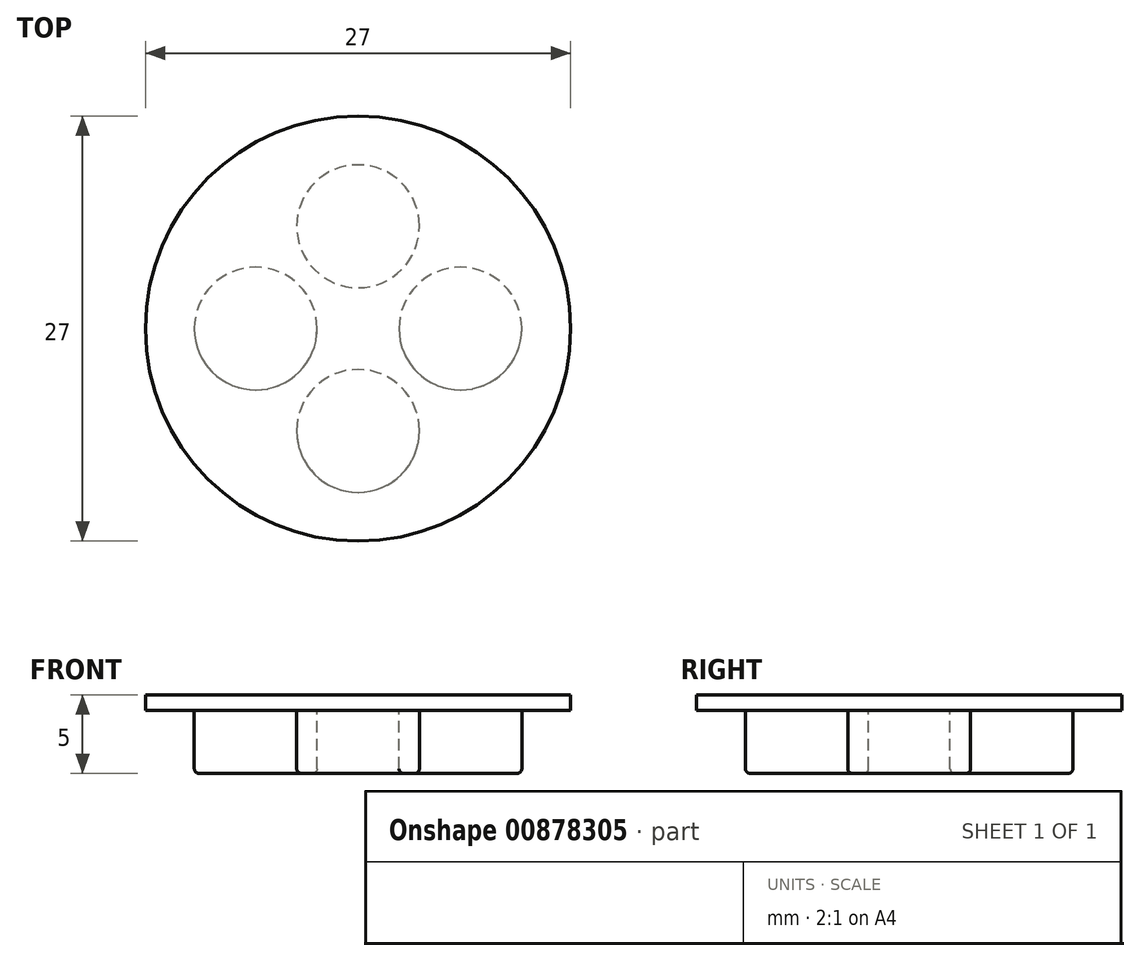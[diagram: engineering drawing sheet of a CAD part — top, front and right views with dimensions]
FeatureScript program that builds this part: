
annotation { "Feature Type Name" : "Feature", "Feature Type Description" : "" }
export const myFeature = defineFeature(function(context is Context, id is Id, definition is map)
    precondition{}
    {
        {
            var Q0;
            Q0=qCreatedBy(makeId("Top.planeOp"),FACE);
            var sketch = newSketch(context, id + "F0", { "sketchPlane" : qUnion([Q0])});
            skCircle(sketch, "E0", {"center": v(-69.13, 46.92) * mm, "radius": 13.5 * mm});
            skSolve(sketch);
        }
        {
            var Q0;
            Q0 = qSketchRegion(id + "F0", true);
            var Q1;
            Q1=makeQuery(id+"F0.imprint","IMPRINT",FACE,{"disambiguationData":[TD([[makeQuery(id+"F0.imprint","IMPRINT",EDGE,{"derivedFrom":sQuery(id+"F0.wireOp",EDGE,"E0")}),1.0]])]});
            extrude(context, id + "F1", {"entities" : qUnion([Q0, Q1]), "depth" : 1 * mm, "offsetDistance" : 25 * mm});
        }
        {
            var Q0;
            Q0=makeQuery(id+"F1.opExtrude","CAP_FACE",FACE,{"disambiguationData":[OSD([sQuery(id+"F0.wireOp",EDGE,"E0")])],"isStart":true});
            var sketch = newSketch(context, id + "F2", { "sketchPlane" : qUnion([Q0])});
            skCircle(sketch, "E1", {"center": v(-69.13, -53.42) * mm, "radius": 3.9 * mm});
            skCircle(sketch, "E2.1.0", {"center": v(-62.63, -46.92) * mm, "radius": 3.9 * mm});
            skCircle(sketch, "E2.2.0", {"center": v(-69.13, -40.42) * mm, "radius": 3.9 * mm});
            skCircle(sketch, "E2.3.0", {"center": v(-75.63, -46.92) * mm, "radius": 3.9 * mm});
            skPoint(sketch, "E2.center", {"position": v(-69.13, -46.92) * mm});
            skSolve(sketch);
        }
        {
            var Q0;
            Q0=makeQuery(id+"F2.imprint","IMPRINT",FACE,{"disambiguationData":[TD([[makeQuery(id+"F2.imprint","IMPRINT",EDGE,{"derivedFrom":sQuery(id+"F2.wireOp",EDGE,"E2.1.0")}),1.0]])]});
            var Q1;
            Q1=makeQuery(id+"F2.imprint","IMPRINT",FACE,{"disambiguationData":[TD([[makeQuery(id+"F2.imprint","IMPRINT",EDGE,{"derivedFrom":sQuery(id+"F2.wireOp",EDGE,"E2.2.0")}),1.0]])]});
            var Q2;
            Q2=makeQuery(id+"F2.imprint","IMPRINT",FACE,{"disambiguationData":[TD([[makeQuery(id+"F2.imprint","IMPRINT",EDGE,{"derivedFrom":sQuery(id+"F2.wireOp",EDGE,"E2.3.0")}),1.0]])]});
            var Q3;
            Q3=makeQuery(id+"F2.imprint","IMPRINT",FACE,{"disambiguationData":[TD([[makeQuery(id+"F2.imprint","IMPRINT",EDGE,{"derivedFrom":sQuery(id+"F2.wireOp",EDGE,"E1")}),1.0]])]});
            extrude(context, id + "F3", {"entities" : qUnion([Q0, Q1, Q2, Q3]), "operationType" : NewBodyOperationType.ADD, "depth" : 4 * mm, "offsetDistance" : 25 * mm});
        }
        {
            var Q0;
            Q0=makeQuery(id+"F3.opExtrude","CAP_EDGE",EDGE,{"disambiguationData":[OSD([sQuery(id+"F2.wireOp",EDGE,"E1")])],"isStart":false});
            var Q1;
            Q1=makeQuery(id+"F3.opExtrude","CAP_EDGE",EDGE,{"disambiguationData":[OSD([sQuery(id+"F2.wireOp",EDGE,"E2.1.0")])],"isStart":false});
            var Q2;
            Q2=makeQuery(id+"F3.opExtrude","CAP_EDGE",EDGE,{"disambiguationData":[OSD([sQuery(id+"F2.wireOp",EDGE,"E2.2.0")])],"isStart":false});
            var Q3;
            Q3=makeQuery(id+"F3.opExtrude","CAP_EDGE",EDGE,{"disambiguationData":[OSD([sQuery(id+"F2.wireOp",EDGE,"E2.3.0")])],"isStart":false});
            fillet(context, id + "F4", {"entities" : qUnion([Q0, Q1, Q2, Q3]), "radius" : 0.3 * mm, "tangentPropagation" : true, "allowEdgeOverflow" : false});
        }
    });
